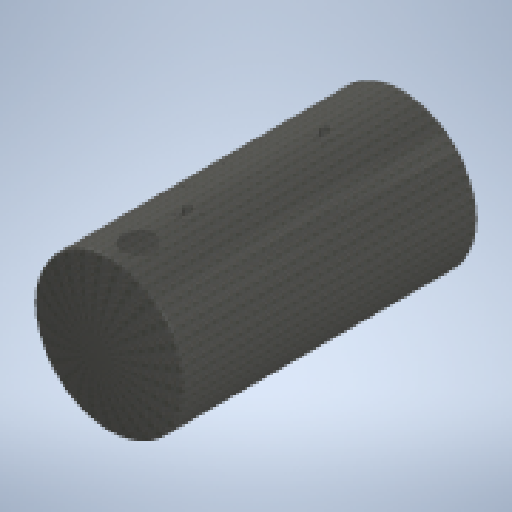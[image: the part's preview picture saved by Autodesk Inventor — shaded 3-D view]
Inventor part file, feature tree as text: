
AUTODESK INVENTOR PART (.ipt)
format: ipt  version: 2023 (Build 270158000, 158)  size: 378,880 bytes
history: native  units: in
note: dims shown in document units (in); Inventor stores cm internally (conversion verified against a paired STEP export)
features: sketch x5, extrude x4, mirror x2, projected_geometry x2, other x1, revolve x1, plane x1
ambient origin geometry x8: Origin, YZ Plane, XZ Plane, XY Plane, X Axis, Y Axis, Z Axis, Center Point
bodies: Solid1 (feature_tree)
feature tree (16):
  other  "CrossSection1"
  extrude  "Extrusion1"  Depth=0.1772in
  revolve  "Revolution2"  [1 undecoded]
  mirror  "Mirror1"
  plane  "Work Plane1"
  extrude  "Extrusion2"  Depth=0.0197in TaperAngle=0.0deg
  extrude  "Extrusion3"  Depth=0.9843in
  extrude  "Extrusion4"  Depth=1.9685in
  mirror  "Mirror2"
  sketch  "Sketch1"  dims[d0=118.1102in d1=0.1772in]
  sketch  "Sketch2"  dims[d2=0.2362in d5=111.4173in]
  projected_geometry  "Projected Loop1"
  sketch  "Sketch3"  dims[d6=216.378in d7=0.0in d8=0.0197in d9=0.0787in d10=0.0in d11=0.7874in]
  sketch  "Sketch4"  dims[d12=0.9843in d13=0.9843in]
  sketch  "Sketch5"  dims[d14=0.9843in d15=1.9685in d16=27.5591in d24=2.5591in d25=12.874in d28=0.9843in d29=90.0deg d30=24.0157in d31=19.685in d32=3.937in d33=0.0in d38=11.811in d39=11.811in d40=51.1811in d41=0.2362in d42=0.3543in d43=0.0in d44=0.0in d45=3.937in d46=3.937in d47=2.9528in d48=7.874in d49=2.3622in d50=1.9685in d51=0.0in]
  projected_geometry  "Projected Loop2"
note: 1 required parameter value undecoded (feature->parameter linkage not recoverable at this tier; creation-order binding heuristic only, values carry confidence <= 0.55)
